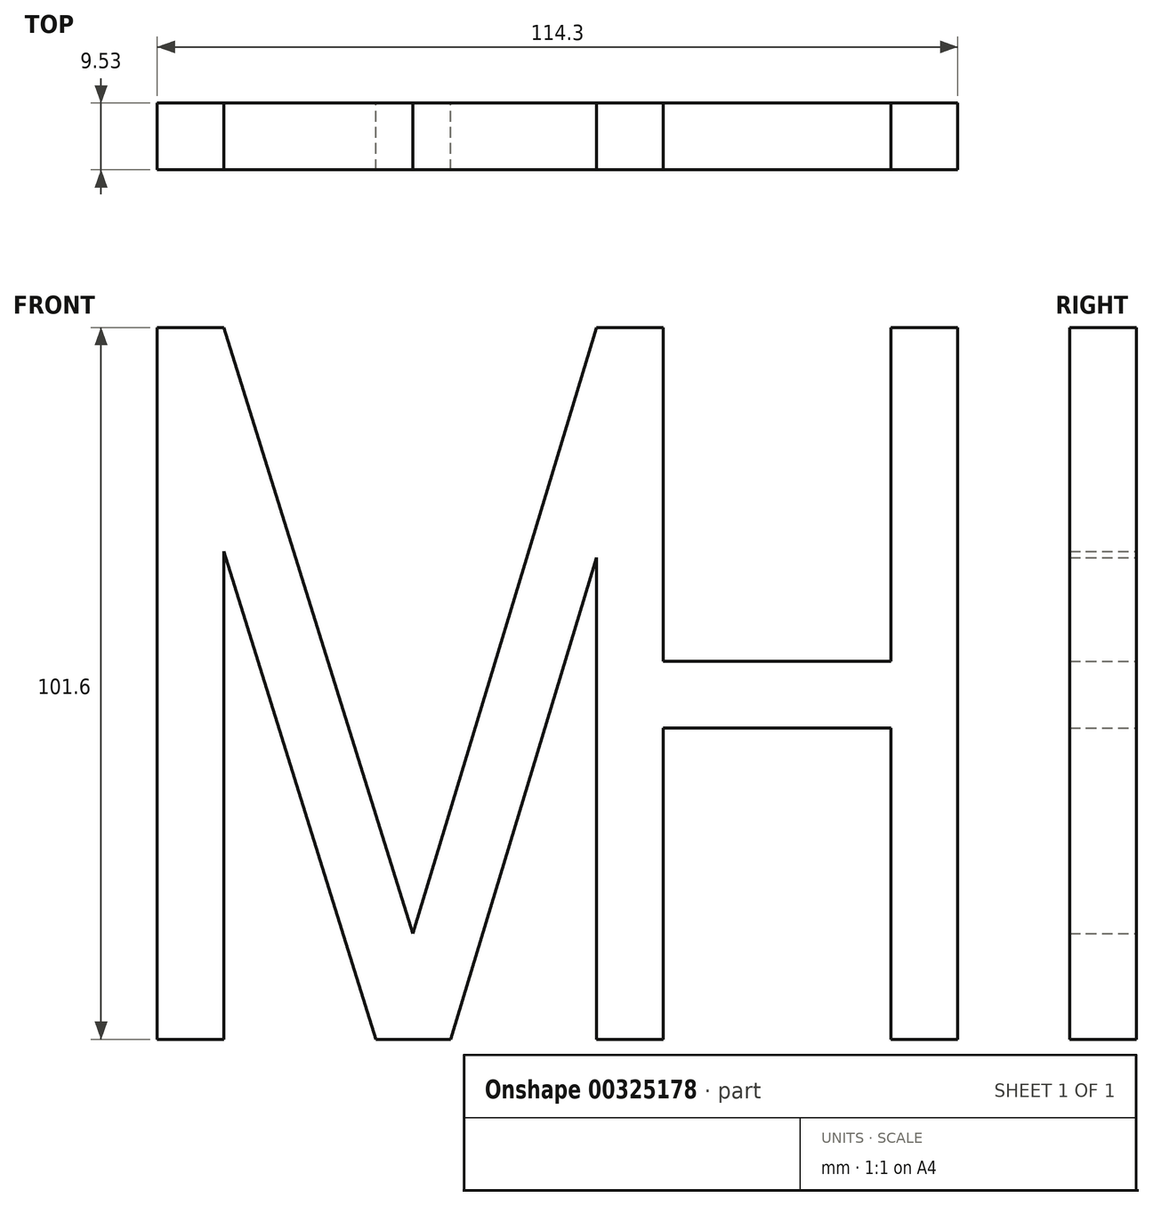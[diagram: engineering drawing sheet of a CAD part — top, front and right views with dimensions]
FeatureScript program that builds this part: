
annotation { "Feature Type Name" : "Feature", "Feature Type Description" : "" }
export const myFeature = defineFeature(function(context is Context, id is Id, definition is map)
    precondition{}
    {
        {
            var Q0;
            Q0=qCreatedBy(makeId("Front.planeOp"),FACE);
            var sketch = newSketch(context, id + "F0", { "sketchPlane" : qUnion([Q0])});
            skLineSegment(sketch, "E0.bottom", {"start": v(0, 0) * mm, "end": v(114.3, 0) * mm});
            skLineSegment(sketch, "E0.top", {"start": v(0, 101.6) * mm, "end": v(114.3, 101.6) * mm});
            skLineSegment(sketch, "E0.left", {"start": v(0, 0) * mm, "end": v(0, 101.6) * mm});
            skLineSegment(sketch, "E0.right", {"start": v(114.3, 0) * mm, "end": v(114.3, 101.6) * mm});
            skLineSegment(sketch, "E1", {"start": v(9.52, 101.6) * mm, "end": v(36.51, 15.08) * mm});
            skLineSegment(sketch, "E2", {"start": v(36.51, 15.08) * mm, "end": v(62.7, 101.6) * mm});
            skLineSegment(sketch, "E3", {"start": v(72.23, 101.6) * mm, "end": v(72.23, 53.97) * mm});
            skLineSegment(sketch, "E4", {"start": v(72.23, 53.97) * mm, "end": v(104.78, 53.98) * mm});
            skLineSegment(sketch, "E5", {"start": v(104.78, 53.98) * mm, "end": v(104.78, 101.6) * mm});
            skLineSegment(sketch, "E6", {"start": v(104.78, 0) * mm, "end": v(104.78, 44.45) * mm});
            skLineSegment(sketch, "E7", {"start": v(104.78, 44.45) * mm, "end": v(72.23, 44.45) * mm});
            skLineSegment(sketch, "E8", {"start": v(72.23, 44.45) * mm, "end": v(72.23, 0) * mm});
            skLineSegment(sketch, "E9", {"start": v(62.7, 0) * mm, "end": v(62.7, 68.73) * mm});
            skLineSegment(sketch, "E10", {"start": v(62.7, 68.73) * mm, "end": v(41.9, 0) * mm});
            skLineSegment(sketch, "E11", {"start": v(9.53, 0) * mm, "end": v(9.52, 69.61) * mm});
            skLineSegment(sketch, "E12", {"start": v(9.52, 69.61) * mm, "end": v(31.24, 0) * mm});
            skSolve(sketch);
        }
        {
            var Q0;
            {var subQ1=sQuery(id+"F0.wireOp",EDGE,"E0.left");Q0=makeQuery(id+"F0.imprint","IMPRINT",FACE,{"disambiguationData":[TD([[makeQuery(id+"F0.imprint","IMPRINT",EDGE,{"derivedFrom":subQ1}),-1.0]])]});}
            extrude(context, id + "F1", {"entities" : qUnion([Q0]), "depth" : 9.52 * mm});
        }
    });
